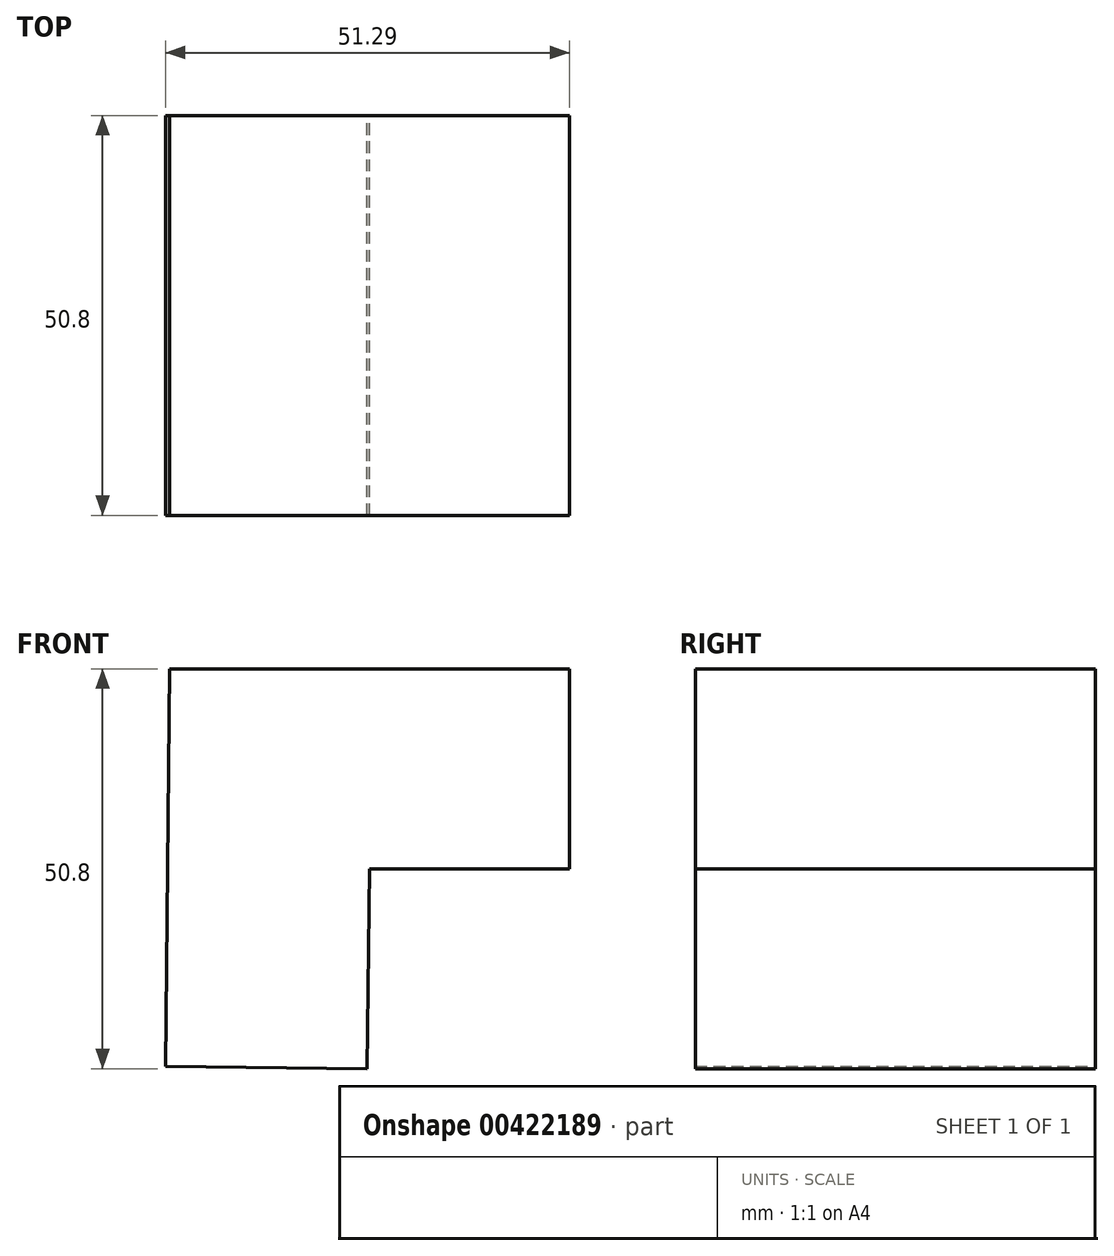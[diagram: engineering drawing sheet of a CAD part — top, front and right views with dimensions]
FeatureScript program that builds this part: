
annotation { "Feature Type Name" : "Feature", "Feature Type Description" : "" }
export const myFeature = defineFeature(function(context is Context, id is Id, definition is map)
    precondition{}
    {
        {
            var Q0;
            Q0=qCreatedBy(makeId("Front.planeOp"),FACE);
            var sketch = newSketch(context, id + "F0", { "sketchPlane" : qUnion([Q0])});
            skLineSegment(sketch, "E0", {"start": v(-25.09, 14.9) * mm, "end": v(25.71, 14.9) * mm});
            skLineSegment(sketch, "E1", {"start": v(1.12, 36.5) * mm, "end": v(0, 36.5) * mm});
            skLineSegment(sketch, "E2", {"start": v(25.71, 14.9) * mm, "end": v(25.71, -10.5) * mm});
            skLineSegment(sketch, "E3", {"start": v(25.71, -10.5) * mm, "end": v(0.31, -10.5) * mm});
            skLineSegment(sketch, "E4", {"start": v(0.31, -10.5) * mm, "end": v(0, -35.9) * mm});
            skLineSegment(sketch, "E5", {"start": v(0, -35.9) * mm, "end": v(-25.58, -35.59) * mm});
            skLineSegment(sketch, "E6", {"start": v(-25.09, 14.9) * mm, "end": v(-25.58, -35.59) * mm});
            skSolve(sketch);
        }
        {
            var Q0;
            Q0 = qSketchRegion(id + "F0", true);
            extrude(context, id + "F1", {"entities" : qUnion([Q0]), "depth" : 50.8 * mm});
        }
    });
